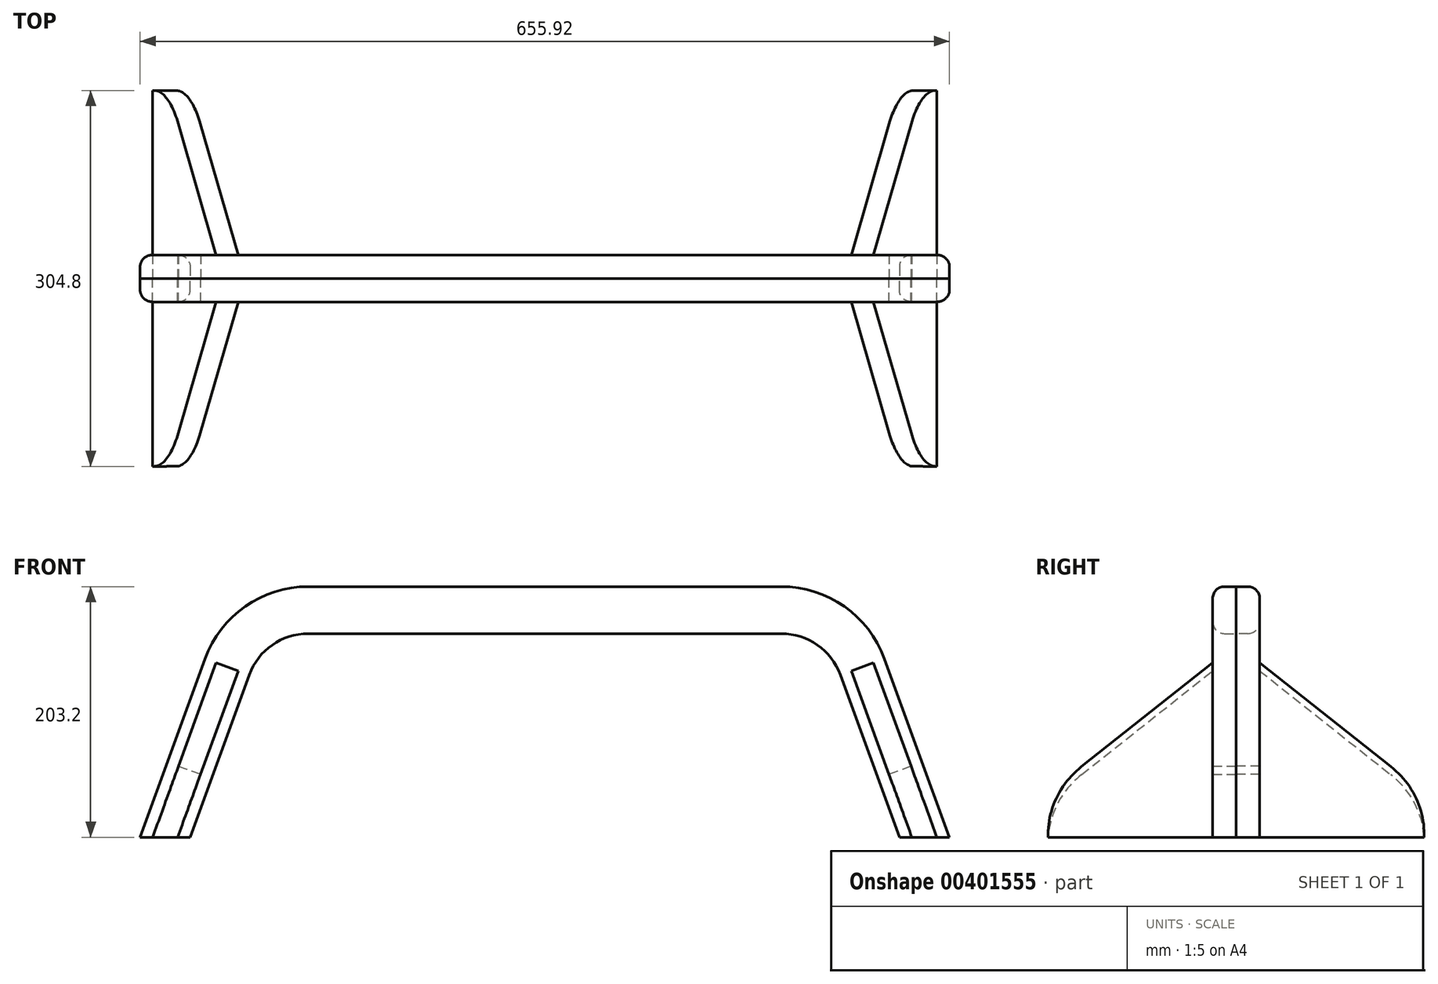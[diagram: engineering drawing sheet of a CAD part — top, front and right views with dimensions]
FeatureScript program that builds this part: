
annotation { "Feature Type Name" : "Feature", "Feature Type Description" : "" }
export const myFeature = defineFeature(function(context is Context, id is Id, definition is map)
    precondition{}
    {
        {
            var Q0;
            Q0=qCreatedBy(makeId("Front.planeOp"),FACE);
            var sketch = newSketch(context, id + "F0", { "sketchPlane" : qUnion([Q0])});
            skLineSegment(sketch, "E0", {"start": v(0, 0) * mm, "end": v(-191.75, 0) * mm});
            skLineSegment(sketch, "E1", {"start": v(-275.3, -58.5) * mm, "end": v(-327.96, -203.2) * mm});
            skLineSegment(sketch, "E2", {"start": v(-327.96, -203.2) * mm, "end": v(-317.82, -203.2) * mm});
            skLineSegment(sketch, "E3", {"start": v(-287.41, -203.2) * mm, "end": v(-239.49, -71.53) * mm});
            skLineSegment(sketch, "E4", {"start": v(-191.75, -38.1) * mm, "end": v(0, -38.1) * mm});
            skPoint(sketch, "E5.visualSharp", {"position": v(-227.32, -38.1) * mm});
            skArc(sketch, "E5.filletArc", {"start": v(-191.75, -38.1) * mm, "mid": v(-220.89, -47.29) * mm, "end": v(-239.49, -71.53) * mm});
            skArc(sketch, "E6.0", {"start": v(-191.75, 0) * mm, "mid": v(-242.74, -16.08) * mm, "end": v(-275.3, -58.5) * mm});
            skPoint(sketch, "E7.orphan", {"position": v(-254, 0) * mm});
            skArc(sketch, "E8.MirrorCS", {"start": v(191.75, 0) * mm, "mid": v(242.74, -16.08) * mm, "end": v(275.3, -58.5) * mm});
            skLineSegment(sketch, "E9.MirrorCS", {"start": v(0, 0) * mm, "end": v(191.75, 0) * mm});
            skLineSegment(sketch, "E10.MirrorCS", {"start": v(191.75, -38.1) * mm, "end": v(0, -38.1) * mm});
            skArc(sketch, "E11.MirrorCS", {"start": v(191.75, -38.1) * mm, "mid": v(220.89, -47.29) * mm, "end": v(239.49, -71.53) * mm});
            skLineSegment(sketch, "E12", {"start": v(-296.9, -145.7) * mm, "end": v(-278.99, -152.2) * mm});
            skLineSegment(sketch, "E13.0", {"start": v(-296.9, -145.7) * mm, "end": v(-317.82, -203.2) * mm});
            skLineSegment(sketch, "E14.0", {"start": v(-278.99, -152.2) * mm, "end": v(-297.55, -203.2) * mm});
            skLineSegment(sketch, "E15.trimOffspring", {"start": v(-297.55, -203.2) * mm, "end": v(-287.41, -203.2) * mm});
            skLineSegment(sketch, "E16.MirrorCS", {"start": v(275.3, -58.5) * mm, "end": v(327.96, -203.2) * mm});
            skLineSegment(sketch, "E17.MirrorCS", {"start": v(327.96, -203.2) * mm, "end": v(317.82, -203.2) * mm});
            skLineSegment(sketch, "E18.MirrorCS", {"start": v(296.9, -145.7) * mm, "end": v(317.82, -203.2) * mm});
            skLineSegment(sketch, "E19.MirrorCS", {"start": v(296.9, -145.7) * mm, "end": v(278.99, -152.2) * mm});
            skLineSegment(sketch, "E20.MirrorCS", {"start": v(278.99, -152.2) * mm, "end": v(297.55, -203.2) * mm});
            skLineSegment(sketch, "E21.MirrorCS", {"start": v(287.41, -203.2) * mm, "end": v(239.49, -71.53) * mm});
            skLineSegment(sketch, "E22.MirrorCS", {"start": v(297.55, -203.2) * mm, "end": v(287.41, -203.2) * mm});
            skSolve(sketch);
        }
        {
            var Q0;
            Q0=makeQuery(id+"F0.imprint","IMPRINT",FACE,{"disambiguationData":[TD([[makeQuery(id+"F0.imprint","IMPRINT",EDGE,{"derivedFrom":sQuery(id+"F0.wireOp",EDGE,"E0")}),1.0]])]});
            extrude(context, id + "F1", {"entities" : qUnion([Q0]), "depth" : 19.05 * mm});
        }
        {
            var Q0;
            Q0=makeQuery(id+"F0.imprint","IMPRINT",FACE,{"disambiguationData":[TD([[makeQuery(id+"F0.imprint","IMPRINT",EDGE,{"derivedFrom":sQuery(id+"F0.wireOp",EDGE,"E0")}),1.0]])]});
            extrude(context, id + "F2", {"entities" : qUnion([Q0]), "oppositeDirection" : true, "depth" : 19.05 * mm});
        }
        {
            var Q0;
            Q0=makeQuery(id+"F1.opExtrude","CAP_EDGE",EDGE,{"disambiguationData":[OSD([sQuery(id+"F0.wireOp",EDGE,"E0"),sQuery(id+"F0.wireOp",EDGE,"E9.MirrorCS")])],"isStart":false});
            var Q1;
            Q1=makeQuery(id+"F1.opExtrude","CAP_EDGE",EDGE,{"disambiguationData":[OSD([sQuery(id+"F0.wireOp",EDGE,"E6.0")])],"isStart":false});
            var Q2;
            Q2=makeQuery(id+"F2.opExtrude","CAP_EDGE",EDGE,{"disambiguationData":[OSD([sQuery(id+"F0.wireOp",EDGE,"E6.0")])],"isStart":false});
            var Q3;
            Q3=makeQuery(id+"F2.opExtrude","CAP_EDGE",EDGE,{"disambiguationData":[OSD([sQuery(id+"F0.wireOp",EDGE,"E0"),sQuery(id+"F0.wireOp",EDGE,"E9.MirrorCS")])],"isStart":false});
            var Q4;
            Q4=makeQuery(id+"F1.opExtrude","CAP_EDGE",EDGE,{"disambiguationData":[OSD([sQuery(id+"F0.wireOp",EDGE,"E4"),sQuery(id+"F0.wireOp",EDGE,"E10.MirrorCS")])],"isStart":false});
            var Q5;
            Q5=makeQuery(id+"F1.opExtrude","CAP_EDGE",EDGE,{"disambiguationData":[OSD([sQuery(id+"F0.wireOp",EDGE,"E5.filletArc")])],"isStart":false});
            var Q6;
            Q6=makeQuery(id+"F1.opExtrude","CAP_EDGE",EDGE,{"disambiguationData":[OSD([sQuery(id+"F0.wireOp",EDGE,"E11.MirrorCS")])],"isStart":false});
            var Q7;
            Q7=makeQuery(id+"F1.opExtrude","CAP_EDGE",EDGE,{"disambiguationData":[OSD([sQuery(id+"F0.wireOp",EDGE,"E8.MirrorCS")])],"isStart":false});
            var Q8;
            Q8=makeQuery(id+"F2.opExtrude","CAP_EDGE",EDGE,{"disambiguationData":[OSD([sQuery(id+"F0.wireOp",EDGE,"E8.MirrorCS")])],"isStart":false});
            var Q9;
            Q9=makeQuery(id+"F2.opExtrude","CAP_EDGE",EDGE,{"disambiguationData":[OSD([sQuery(id+"F0.wireOp",EDGE,"E11.MirrorCS")])],"isStart":false});
            var Q10;
            Q10=makeQuery(id+"F2.opExtrude","CAP_EDGE",EDGE,{"disambiguationData":[OSD([sQuery(id+"F0.wireOp",EDGE,"E4"),sQuery(id+"F0.wireOp",EDGE,"E10.MirrorCS")])],"isStart":false});
            fillet(context, id + "F3", {"entities" : qUnion([Q0, Q1, Q2, Q3, Q4, Q5, Q6, Q7, Q8, Q9, Q10]), "radius" : 9.52 * mm, "tangentPropagation" : true, "allowEdgeOverflow" : false});
        }
        {
            var Q0;
            {var subQ0=sQuery(id+"F0.wireOp",EDGE,"E13.0");Q0=makeQuery(id+"F2.boolean.opBoolean","MERGE",FACE,{"derivedFrom":[makeQuery(id+"F1.opExtrude","SWEPT_FACE",FACE,{"disambiguationData":[OSD([subQ0])]}),makeQuery(id+"F2.opExtrude","SWEPT_FACE",FACE,{"disambiguationData":[OSD([subQ0])]})]});}
            var sketch = newSketch(context, id + "F4", { "sketchPlane" : qUnion([Q0])});
            skLineSegment(sketch, "E23", {"start": v(-152.4, -299.65) * mm, "end": v(152.4, -299.65) * mm});
            skLineSegment(sketch, "E24.0.2", {"start": v(19.05, -238.45) * mm, "end": v(-19.05, -238.45) * mm});
            skLineSegment(sketch, "E25", {"start": v(-152.4, -299.65) * mm, "end": v(-152.4, -296.97) * mm});
            skLineSegment(sketch, "E26", {"start": v(152.4, -299.65) * mm, "end": v(152.4, -296.97) * mm});
            skPoint(sketch, "E27.0", {"position": v(-19.05, -149.12) * mm});
            skPoint(sketch, "E28.0", {"position": v(19.05, -149.12) * mm});
            skLineSegment(sketch, "E29", {"start": v(-125.32, -238.71) * mm, "end": v(-19.05, -149.12) * mm});
            skLineSegment(sketch, "E30", {"start": v(-19.05, -238.45) * mm, "end": v(-19.05, -149.12) * mm});
            skLineSegment(sketch, "E31", {"start": v(19.05, -238.45) * mm, "end": v(19.05, -149.12) * mm});
            skLineSegment(sketch, "E32", {"start": v(19.05, -149.12) * mm, "end": v(125.32, -238.71) * mm});
            skPoint(sketch, "E33.visualSharp", {"position": v(-152.4, -261.55) * mm});
            skArc(sketch, "E33.filletArc", {"start": v(-125.32, -238.71) * mm, "mid": v(-145.3, -264.85) * mm, "end": v(-152.4, -296.97) * mm});
            skPoint(sketch, "E34.visualSharp", {"position": v(152.4, -261.55) * mm});
            skArc(sketch, "E34.filletArc", {"start": v(152.4, -296.97) * mm, "mid": v(145.3, -264.85) * mm, "end": v(125.32, -238.71) * mm});
            skSolve(sketch);
        }
        {
            var Q0;
            Q0=makeQuery(id+"F4.imprint","IMPRINT",FACE,{"disambiguationData":[TD([[makeQuery(id+"F4.imprint","IMPRINT",EDGE,{"derivedFrom":sQuery(id+"F4.wireOp",EDGE,"E24.0.2")}),-1.0]])]});
            var Q1;
            {var subQ0=sQuery(id+"F4.wireOp",EDGE,"E25");Q1=makeQuery(id+"F4.imprint","IMPRINT",FACE,{"disambiguationData":[TD([[makeQuery(id+"F4.imprint","IMPRINT",EDGE,{"derivedFrom":subQ0}),-1.0]])]});}
            var Q2;
            {var subQ0=sQuery(id+"F4.wireOp",EDGE,"E26");Q2=makeQuery(id+"F4.imprint","IMPRINT",FACE,{"disambiguationData":[TD([[makeQuery(id+"F4.imprint","IMPRINT",EDGE,{"derivedFrom":subQ0}),1.0]])]});}
            var Q3;
            {var subQ1=sQuery(id+"F0.wireOp",EDGE,"E13.0");var subQ2=makeQuery(id+"F1.opExtrude","CAP_EDGE",EDGE,{"disambiguationData":[OSD([subQ1])],"isStart":true});Q3=makeQuery(id+"F4.imprint","IMPRINT",FACE,{"disambiguationData":[TD([[makeQuery(id+"F4.imprint","IMPRINT",EDGE,{"derivedFrom":subQ2}),1.0]])]});}
            extrude(context, id + "F5", {"entities" : qUnion([Q0, Q1, Q2, Q3]), "depth" : 19.05 * mm});
        }
        {
            var Q0;
            {var subQ0=sQuery(id+"F0.wireOp",EDGE,"E15.trimOffspring");Q0=makeQuery(id+"F2.boolean.opBoolean","MERGE",FACE,{"derivedFrom":[makeQuery(id+"F1.opExtrude","SWEPT_FACE",FACE,{"disambiguationData":[OSD([subQ0])]}),makeQuery(id+"F2.opExtrude","SWEPT_FACE",FACE,{"disambiguationData":[OSD([subQ0])]})]});}
            var sketch = newSketch(context, id + "F6", { "sketchPlane" : qUnion([Q0])});
            skLineSegment(sketch, "E35.bottom", {"start": v(-236.12, 155.93) * mm, "end": v(-390.84, 155.93) * mm});
            skLineSegment(sketch, "E35.top", {"start": v(-236.12, -167.08) * mm, "end": v(-390.84, -167.08) * mm});
            skLineSegment(sketch, "E35.left", {"start": v(-236.12, 155.93) * mm, "end": v(-236.12, -167.08) * mm});
            skLineSegment(sketch, "E35.right", {"start": v(-390.84, 155.93) * mm, "end": v(-390.84, -167.08) * mm});
            skSolve(sketch);
        }
        {
            var Q0;
            Q0 = qSketchRegion(id + "F6", true);
            extrude(context, id + "F7", {"entities" : qUnion([Q0]), "operationType" : NewBodyOperationType.REMOVE, "depth" : 25.4 * mm});
        }
        {
            var Q0;
            Q0=makeQuery(id+"F5.opExtrude","SWEPT_BODY",BODY,{"disambiguationData":[OSD([sQuery(id+"F4.wireOp",EDGE,"E23"),sQuery(id+"F4.wireOp",EDGE,"E24.0.2"),sQuery(id+"F4.wireOp",EDGE,"E25"),sQuery(id+"F4.wireOp",EDGE,"E26"),sQuery(id+"F4.wireOp",EDGE,"E29"),sQuery(id+"F4.wireOp",EDGE,"E30"),sQuery(id+"F4.wireOp",EDGE,"E31"),sQuery(id+"F4.wireOp",EDGE,"E32"),sQuery(id+"F4.wireOp",EDGE,"E33.filletArc"),sQuery(id+"F4.wireOp",EDGE,"E34.filletArc")])]});
            var Q1;
            Q1=qCreatedBy(makeId("Right.planeOp"),FACE);
            mirror(context, id + "F8", {"entities" : qUnion([Q0]), "mirrorPlane" : qUnion([Q1])});
        }
    });
